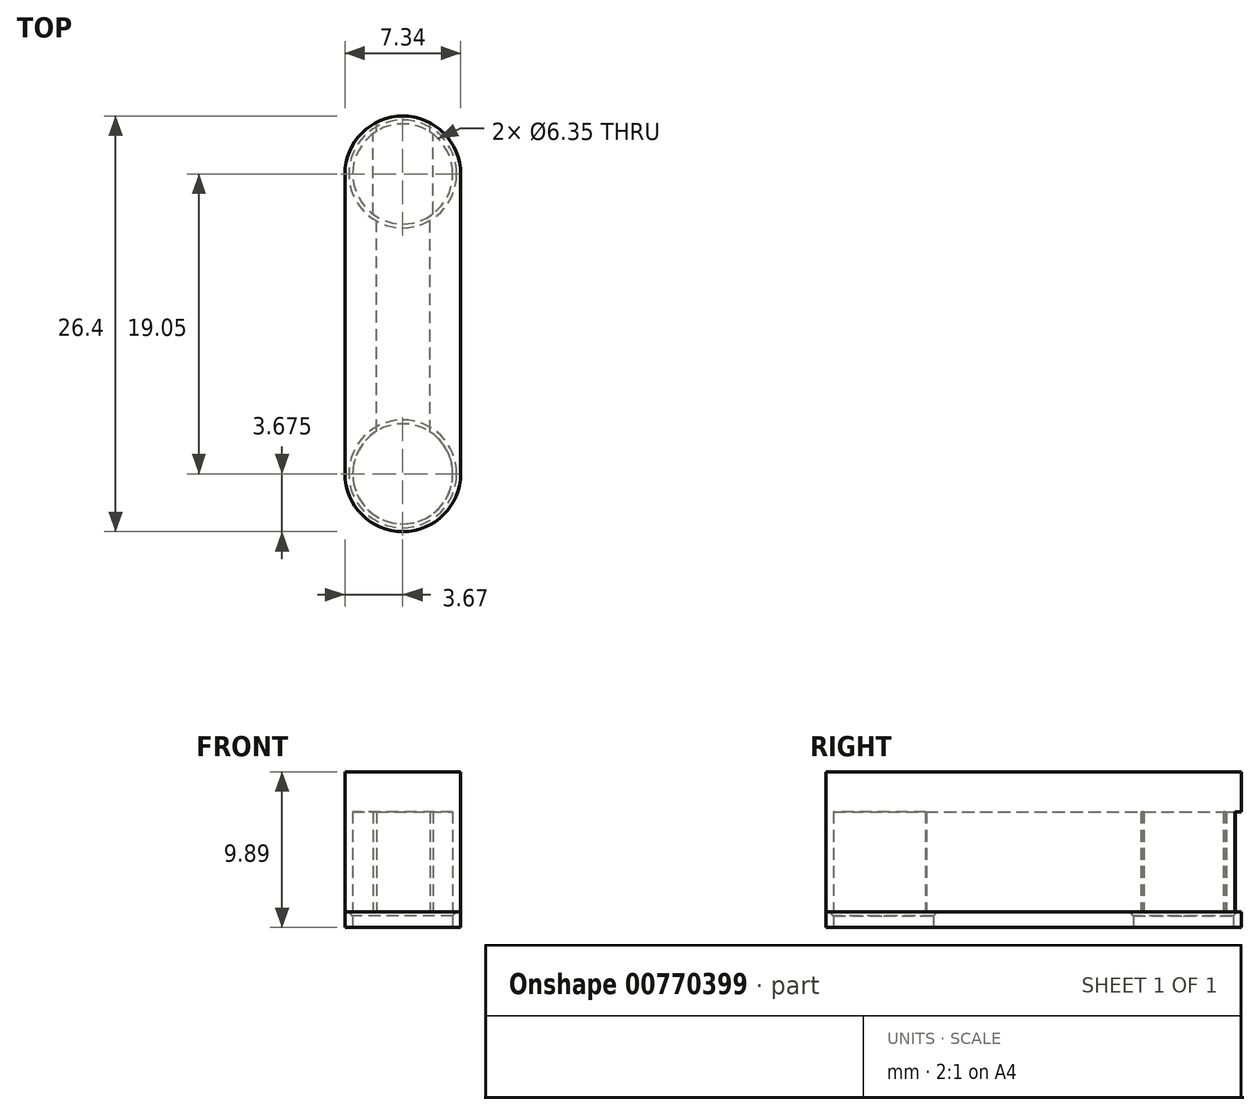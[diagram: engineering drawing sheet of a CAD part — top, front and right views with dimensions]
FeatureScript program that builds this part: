
annotation { "Feature Type Name" : "Feature", "Feature Type Description" : "" }
export const myFeature = defineFeature(function(context is Context, id is Id, definition is map)
    precondition{}
    {
        {
            var Q0;
            Q0=qCreatedBy(makeId("Top.planeOp"),FACE);
            var sketch = newSketch(context, id + "F0", { "sketchPlane" : qUnion([Q0])});
            skLineSegment(sketch, "E0.bottom", {"start": v(3.17, -12.7) * mm, "end": v(-3.18, -12.7) * mm, "construction": true});
            skLineSegment(sketch, "E0.top", {"start": v(3.18, 12.7) * mm, "end": v(-3.17, 12.7) * mm, "construction": true});
            skLineSegment(sketch, "E0.left", {"start": v(3.17, -12.7) * mm, "end": v(3.18, 12.7) * mm, "construction": true});
            skLineSegment(sketch, "E0.right", {"start": v(-3.18, -12.7) * mm, "end": v(-3.17, 12.7) * mm, "construction": true});
            skLineSegment(sketch, "E1", {"start": v(3.18, 0) * mm, "end": v(-3.18, 0) * mm, "construction": true});
            skLineSegment(sketch, "E2.bottom", {"start": v(6.35, -6.35) * mm, "end": v(-6.35, -6.35) * mm, "construction": true});
            skLineSegment(sketch, "E2.top", {"start": v(6.35, 6.35) * mm, "end": v(-6.35, 6.35) * mm, "construction": true});
            skPoint(sketch, "E2.middle", {"position": v(0, 0) * mm});
            skPoint(sketch, "E3", {"position": v(0, 6.35) * mm});
            skLineSegment(sketch, "E4", {"start": v(0, 12.7) * mm, "end": v(0, 6.35) * mm, "construction": true});
            skPoint(sketch, "E5", {"position": v(0, -6.35) * mm});
            skLineSegment(sketch, "E6", {"start": v(0, -6.35) * mm, "end": v(0, -12.7) * mm, "construction": true});
            skCircle(sketch, "E7", {"center": v(0, 9.53) * mm, "radius": 3.18 * mm});
            skCircle(sketch, "E8", {"center": v(0, -9.53) * mm, "radius": 3.18 * mm});
            skCircle(sketch, "E9", {"center": v(0, 9.53) * mm, "radius": 3.67 * mm});
            skCircle(sketch, "E10", {"center": v(0, -9.53) * mm, "radius": 3.67 * mm});
            skPoint(sketch, "E11", {"position": v(-3.67, 9.53) * mm});
            skPoint(sketch, "E12", {"position": v(3.68, 9.53) * mm});
            skPoint(sketch, "E13", {"position": v(3.68, -9.53) * mm});
            skPoint(sketch, "E14", {"position": v(-3.67, -9.53) * mm});
            skLineSegment(sketch, "E15", {"start": v(-3.67, 9.53) * mm, "end": v(-3.67, -9.53) * mm});
            skLineSegment(sketch, "E16", {"start": v(3.68, -9.53) * mm, "end": v(3.68, 9.53) * mm});
            skSolve(sketch);
        }
        {
            var Q0;
            {var subQ0=sQuery(id+"F0.wireOp",EDGE,"E15");Q0=makeQuery(id+"F0.imprint","IMPRINT",FACE,{"disambiguationData":[TD([[makeQuery(id+"F0.imprint","IMPRINT",EDGE,{"derivedFrom":subQ0}),1.0]])]});}
            var Q1;
            Q1=makeQuery(id+"F0.imprint","IMPRINT",FACE,{"disambiguationData":[TD([[makeQuery(id+"F0.imprint","IMPRINT",EDGE,{"derivedFrom":sQuery(id+"F0.wireOp",EDGE,"E7")}),-1.0]])]});
            var Q2;
            Q2=makeQuery(id+"F0.imprint","IMPRINT",FACE,{"disambiguationData":[TD([[makeQuery(id+"F0.imprint","IMPRINT",EDGE,{"derivedFrom":sQuery(id+"F0.wireOp",EDGE,"E8")}),-1.0]])]});
            extrude(context, id + "F1", {"entities" : qUnion([Q0, Q1, Q2]), "depth" : 1 * mm, "offsetDistance" : 25 * mm});
        }
        {
            var Q0;
            Q0=makeQuery(id+"F1.opExtrude","CAP_EDGE",EDGE,{"disambiguationData":[OSD([sQuery(id+"F0.wireOp",EDGE,"E8")])],"isStart":false});
            var Q1;
            Q1=makeQuery(id+"F1.opExtrude","CAP_EDGE",EDGE,{"disambiguationData":[OSD([sQuery(id+"F0.wireOp",EDGE,"E7")])],"isStart":false});
            chamfer(context, id + "F2", {"entities" : qUnion([Q0, Q1]), "width" : .25 * mm, "tangentPropagation" : true});
        }
        {
            var Q0;
            Q0=makeQuery(id+"F0.imprint","IMPRINT",FACE,{"disambiguationData":[TD([[makeQuery(id+"F0.imprint","IMPRINT",EDGE,{"derivedFrom":sQuery(id+"F0.wireOp",EDGE,"E7")}),-1.0]])]});
            var Q1;
            Q1=makeQuery(id+"F0.imprint","IMPRINT",FACE,{"disambiguationData":[TD([[makeQuery(id+"F0.imprint","IMPRINT",EDGE,{"derivedFrom":sQuery(id+"F0.wireOp",EDGE,"E7")}),1.0]])]});
            var Q2;
            {var subQ0=sQuery(id+"F0.wireOp",EDGE,"E15");Q2=makeQuery(id+"F0.imprint","IMPRINT",FACE,{"disambiguationData":[TD([[makeQuery(id+"F0.imprint","IMPRINT",EDGE,{"derivedFrom":subQ0}),1.0]])]});}
            var Q3;
            Q3=makeQuery(id+"F0.imprint","IMPRINT",FACE,{"disambiguationData":[TD([[makeQuery(id+"F0.imprint","IMPRINT",EDGE,{"derivedFrom":sQuery(id+"F0.wireOp",EDGE,"E8")}),-1.0]])]});
            var Q4;
            Q4=makeQuery(id+"F0.imprint","IMPRINT",FACE,{"disambiguationData":[TD([[makeQuery(id+"F0.imprint","IMPRINT",EDGE,{"derivedFrom":sQuery(id+"F0.wireOp",EDGE,"E8")}),1.0]])]});
            extrude(context, id + "F3", {"entities" : qUnion([Q0, Q1, Q2, Q3, Q4]), "depth" : 8.9 * mm, "offsetDistance" : 25 * mm});
        }
        {
            var Q0;
            Q0=makeQuery(id+"F3.opExtrude","SWEPT_BODY",BODY,{"disambiguationData":[OSD([sQuery(id+"F0.wireOp",EDGE,"E9"),sQuery(id+"F0.wireOp",EDGE,"E10"),sQuery(id+"F0.wireOp",EDGE,"E15"),sQuery(id+"F0.wireOp",EDGE,"E16")])]});
            transform(context, id + "F4", {"entities" : qUnion([Q0]), "transformType" : TransformType.TRANSLATION_3D, "dx" : 0 * mm, "dy" : 0 * mm, "dz" : 1 * mm, "makeCopy" : false});
        }
        {
            var Q0;
            Q0=makeQuery(id+"F3.opExtrude","CAP_FACE",FACE,{"disambiguationData":[OSD([sQuery(id+"F0.wireOp",EDGE,"E9"),sQuery(id+"F0.wireOp",EDGE,"E10"),sQuery(id+"F0.wireOp",EDGE,"E15"),sQuery(id+"F0.wireOp",EDGE,"E16")])],"isStart":true});
            var sketch = newSketch(context, id + "F5", { "sketchPlane" : qUnion([Q0])});
            skCircle(sketch, "E17", {"center": v(0, 9.53) * mm, "radius": 3.18 * mm});
            skCircle(sketch, "E18", {"center": v(0, -9.53) * mm, "radius": 3.18 * mm});
            skLineSegment(sketch, "E19.bottom", {"start": v(1.93, 7.95) * mm, "end": v(-1.88, 7.95) * mm});
            skLineSegment(sketch, "E19.top", {"start": v(1.93, -19.7) * mm, "end": v(-1.88, -19.7) * mm});
            skLineSegment(sketch, "E19.left", {"start": v(1.93, 7.95) * mm, "end": v(1.93, -19.7) * mm});
            skLineSegment(sketch, "E19.right", {"start": v(-1.88, 7.95) * mm, "end": v(-1.88, -19.7) * mm});
            skSolve(sketch);
        }
        {
            var Q0;
            Q0=makeQuery(id+"F5.imprint","IMPRINT",FACE,{"disambiguationData":[TD([[makeQuery(id+"F5.imprint","IMPRINT",EDGE,{"derivedFrom":sQuery(id+"F5.wireOp",EDGE,"E17")}),1.0]])]});
            var Q1;
            Q1=makeQuery(id+"F5.imprint","IMPRINT",FACE,{"disambiguationData":[TD([[makeQuery(id+"F5.imprint","IMPRINT",EDGE,{"derivedFrom":sQuery(id+"F5.wireOp",EDGE,"E18")}),1.0]])]});
            var Q2;
            {var subQ0=sQuery(id+"F5.wireOp",EDGE,"E19.left");var subQ1=sQuery(id+"F5.wireOp",EDGE,"E18");var subQ2=makeQuery(id+"F5.imprint","INTERSECT",VERTEX,{"disambiguationData":[OD(0.0)],"derivedFrom":[subQ1,subQ0]});Q2=makeQuery(id+"F5.imprint","IMPRINT",FACE,{"disambiguationData":[TD([[makeQuery(id+"F5.imprint","IMPRINT",EDGE,{"disambiguationData":[TD([[subQ2,1.0]])],"derivedFrom":subQ1}),1.0]])]});}
            var Q3;
            {var subQ0=sQuery(id+"F5.wireOp",EDGE,"E19.right");var subQ1=sQuery(id+"F5.wireOp",EDGE,"E18");var subQ2=makeQuery(id+"F5.imprint","INTERSECT",VERTEX,{"disambiguationData":[OD(0.0)],"derivedFrom":[subQ1,subQ0]});Q3=makeQuery(id+"F5.imprint","IMPRINT",FACE,{"disambiguationData":[TD([[makeQuery(id+"F5.imprint","IMPRINT",EDGE,{"disambiguationData":[TD([[subQ2,-1.0]])],"derivedFrom":subQ1}),1.0]])]});}
            extrude(context, id + "F6", {"entities" : qUnion([Q0, Q1, Q2, Q3]), "operationType" : NewBodyOperationType.REMOVE, "oppositeDirection" : true, "depth" : 6.35 * mm, "offsetDistance" : 25 * mm});
        }
        {
            var Q0;
            Q0=makeQuery(id+"F3.opExtrude","CAP_FACE",FACE,{"disambiguationData":[OSD([sQuery(id+"F0.wireOp",EDGE,"E9"),sQuery(id+"F0.wireOp",EDGE,"E10"),sQuery(id+"F0.wireOp",EDGE,"E15"),sQuery(id+"F0.wireOp",EDGE,"E16")])],"isStart":true});
            var sketch = newSketch(context, id + "F7", { "sketchPlane" : qUnion([Q0])});
            skLineSegment(sketch, "E20.bottom", {"start": v(1.73, 9.9) * mm, "end": v(-1.66, 9.9) * mm});
            skLineSegment(sketch, "E20.top", {"start": v(1.73, -17.76) * mm, "end": v(-1.66, -17.76) * mm});
            skLineSegment(sketch, "E20.left", {"start": v(1.73, 9.9) * mm, "end": v(1.73, -17.76) * mm});
            skLineSegment(sketch, "E20.right", {"start": v(-1.66, 9.9) * mm, "end": v(-1.66, -17.76) * mm});
            skSolve(sketch);
        }
        {
            var Q0;
            {var subQ0=sQuery(id+"F7.wireOp",EDGE,"E20.bottom");Q0=makeQuery(id+"F7.imprint","IMPRINT",FACE,{"disambiguationData":[TD([[makeQuery(id+"F7.imprint","IMPRINT",EDGE,{"derivedFrom":subQ0}),1.0]])]});}
            var Q1;
            {var subQ0=sQuery(id+"F7.wireOp",EDGE,"E20.left");var subQ1=makeQuery(id+"F6.boolean.opBoolean","COPY",EDGE,{"derivedFrom":makeQuery(id+"F6.opExtrude","CAP_EDGE",EDGE,{"disambiguationData":[OSD([sQuery(id+"F5.wireOp",EDGE,"E17")])],"isStart":true})});var subQ2=makeQuery(id+"F7.imprint","INTERSECT",VERTEX,{"derivedFrom":[subQ1,subQ0]});Q1=makeQuery(id+"F7.imprint","IMPRINT",FACE,{"disambiguationData":[TD([[makeQuery(id+"F7.imprint","IMPRINT",EDGE,{"disambiguationData":[TD([[subQ2,-1.0]])],"derivedFrom":subQ0}),-1.0]])]});}
            var Q2;
            {var subQ0=sQuery(id+"F7.wireOp",EDGE,"E20.left");var subQ1=makeQuery(id+"F6.boolean.opBoolean","COPY",EDGE,{"derivedFrom":makeQuery(id+"F6.opExtrude","CAP_EDGE",EDGE,{"disambiguationData":[OSD([sQuery(id+"F5.wireOp",EDGE,"E18")])],"isStart":true})});var subQ2=makeQuery(id+"F7.imprint","INTERSECT",VERTEX,{"disambiguationData":[OD(0.0)],"derivedFrom":[subQ1,subQ0]});Q2=makeQuery(id+"F7.imprint","IMPRINT",FACE,{"disambiguationData":[TD([[makeQuery(id+"F7.imprint","IMPRINT",EDGE,{"disambiguationData":[TD([[subQ2,-1.0]])],"derivedFrom":subQ0}),-1.0]])]});}
            var Q3;
            {var subQ0=sQuery(id+"F7.wireOp",EDGE,"E20.left");var subQ1=makeQuery(id+"F3.opExtrude","CAP_EDGE",EDGE,{"disambiguationData":[OSD([sQuery(id+"F0.wireOp",EDGE,"E9")])],"isStart":true});var subQ2=makeQuery(id+"F7.imprint","INTERSECT",VERTEX,{"derivedFrom":[subQ1,subQ0]});Q3=makeQuery(id+"F7.imprint","IMPRINT",FACE,{"disambiguationData":[TD([[makeQuery(id+"F7.imprint","IMPRINT",EDGE,{"disambiguationData":[TD([[subQ2,1.0]])],"derivedFrom":subQ0}),-1.0]])]});}
            var Q4;
            {var subQ0=sQuery(id+"F7.wireOp",EDGE,"E20.top");Q4=makeQuery(id+"F7.imprint","IMPRINT",FACE,{"disambiguationData":[TD([[makeQuery(id+"F7.imprint","IMPRINT",EDGE,{"derivedFrom":subQ0}),-1.0]])]});}
            extrude(context, id + "F8", {"entities" : qUnion([Q0, Q1, Q2, Q3, Q4]), "operationType" : NewBodyOperationType.REMOVE, "oppositeDirection" : true, "depth" : 6.35 * mm, "offsetDistance" : 25 * mm});
        }
    });
